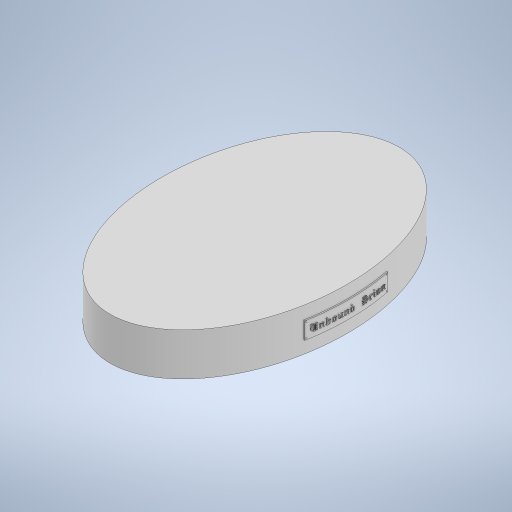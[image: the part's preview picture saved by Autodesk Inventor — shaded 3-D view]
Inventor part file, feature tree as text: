
AUTODESK INVENTOR PART (.ipt)
format: ipt  version: 2024 (Build 280153000, 153)  size: 3,688,448 bytes
history: native  units: mm
features: split x27, thicken_offset x19, sketch x4, extrude x2, plane x1, fillet x1, other x1
ambient origin geometry x8: Origin, YZ Plane, XZ Plane, XY Plane, X Axis, Y Axis, Z Axis, Center Point
bodies: Solid1 (feature_tree)
feature tree (55):
  extrude  "Extrusion1"  Depth=54.5mm
  extrude  "Extrusion2"  Depth=51.0mm
  plane  "Work Plane2"
  sketch  "Sketch4"  dims[d6=3.0mm d7=0.0mm d9=80.0mm d10=32.748225mm d13=5.920965mm d14=10.0mm d16=49.0mm d18=0.75mm d19=0.75mm d20=0.75mm d21=0.75mm d22=0.75mm d23=0.75mm d25=0.75mm d26=0.75mm d27=0.75mm d28=0.75mm d29=0.75mm d30=0.75mm d31=0.5mm d32=0.5mm d33=0.5mm d34=0.5mm d35=0.5mm d36=0.5mm d37=0.5mm d38=0.5mm d39=0.5mm d40=0.5mm d41=0.5mm d42=0.5mm d43=0.5mm d44=0.5mm d45=0.5mm d46=0.5mm d47=0.5mm d48=0.5mm d49=0.5mm d50=0.5mm d51=0.5mm d52=0.5mm d53=0.5mm d54=0.5mm d55=0.5mm d56=0.5mm d57=0.5mm d58=0.5mm d59=0.4mm d60=0.4mm d61=0.4mm d62=0.4mm d63=0.4mm d64=0.4mm d65=0.4mm d66=0.4mm d67=0.35mm]
  sketch  "3D Sketch1"
  split  "Split1"
  split  "Split2"
  split  "Split3"
  split  "Split4"
  split  "Split5"
  split  "Split6"
  split  "Split7"
  split  "Split8"
  split  "Split9"
  split  "Split10"
  split  "Split11"
  split  "Split12"
  split  "Split13"
  split  "Split14"
  split  "Split15"
  split  "Split16"
  split  "Split17"
  split  "Split18"
  split  "Split19"
  split  "Split20"
  split  "Split21"
  split  "Split22"
  split  "Split23"
  split  "Split24"
  split  "Split25"
  split  "Split26"
  split  "Split27"
  thicken_offset  "Thicken1"
  thicken_offset  "Thicken2"
  thicken_offset  "Thicken3"
  thicken_offset  "Thicken4"
  thicken_offset  "Thicken5"
  thicken_offset  "Thicken6"
  thicken_offset  "Thicken7"
  thicken_offset  "Thicken8"
  thicken_offset  "Thicken9"
  thicken_offset  "Thicken10"
  thicken_offset  "Thicken11"
  thicken_offset  "Thicken12"
  thicken_offset  "Thicken13"
  thicken_offset  "Thicken14"
  thicken_offset  "Thicken15"
  thicken_offset  "Thicken16"
  thicken_offset  "Thicken17"
  thicken_offset  "Thicken18"
  thicken_offset  "Thicken19"
  fillet  "Fillet1"  Radius=22.0mm
  sketch  "Sketch1"  dims[d0=85.0mm d1=54.5mm]
  sketch  "Sketch2"  dims[d2=81.5mm d3=51.0mm d4=22.0mm d5=0.0mm]
  other  "Project to Surface1"
